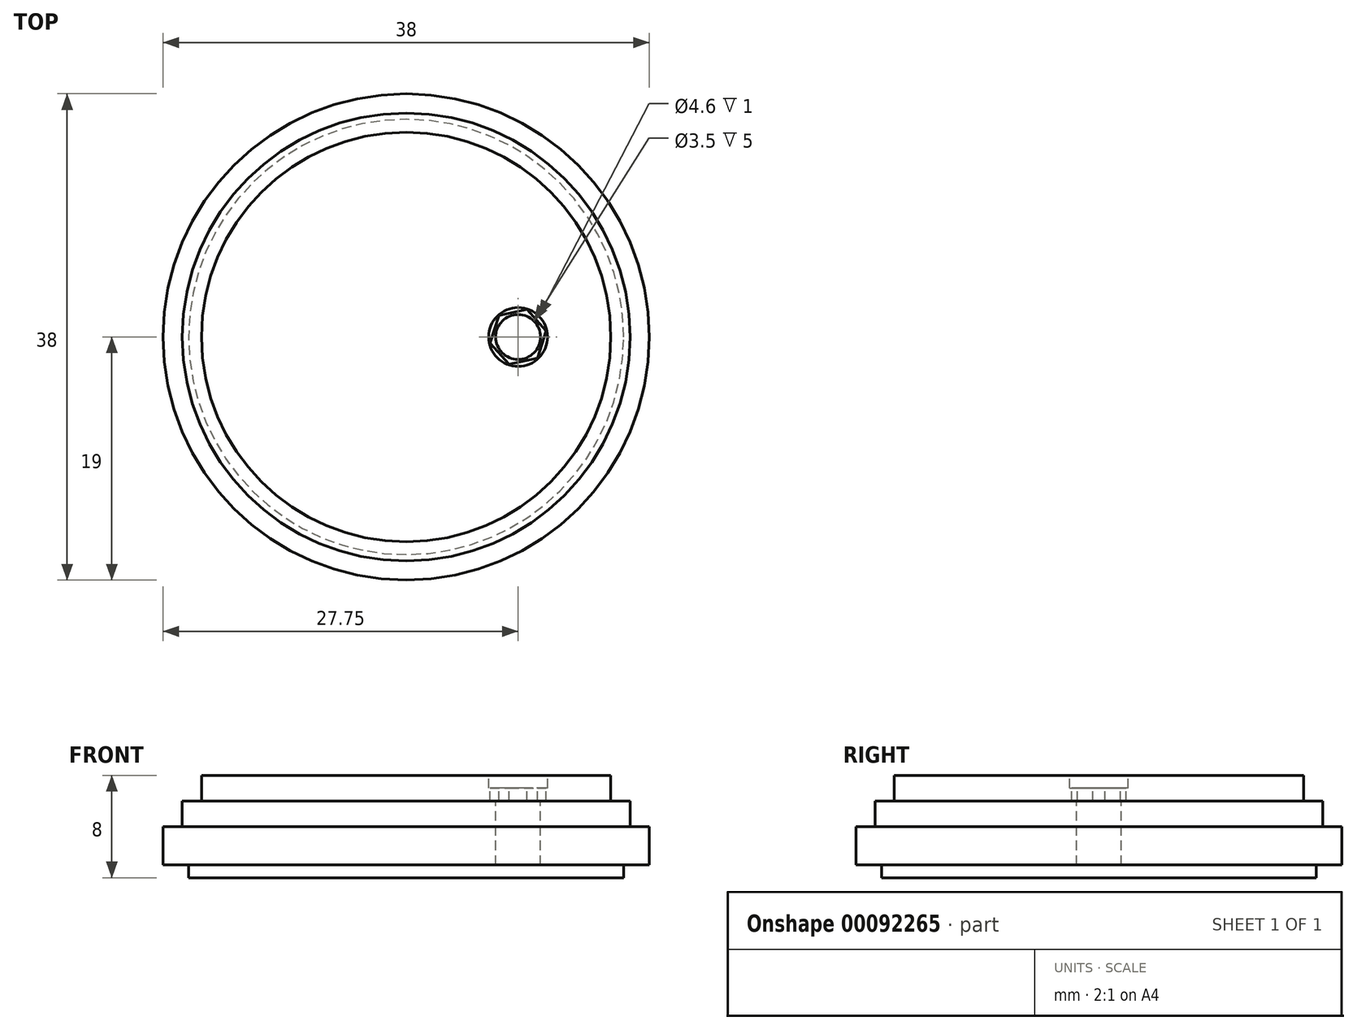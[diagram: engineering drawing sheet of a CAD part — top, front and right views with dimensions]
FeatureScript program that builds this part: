
annotation { "Feature Type Name" : "Feature", "Feature Type Description" : "" }
export const myFeature = defineFeature(function(context is Context, id is Id, definition is map)
    precondition{}
    {
        {
            var Q0;
            Q0=qCreatedBy(makeId("Front.planeOp"),FACE);
            var sketch = newSketch(context, id + "F0", { "sketchPlane" : qUnion([Q0])});
            skLineSegment(sketch, "E0", {"start": v(0, 0) * mm, "end": v(0, 8) * mm});
            skLineSegment(sketch, "E1", {"start": v(0, 8) * mm, "end": v(16, 8) * mm});
            skLineSegment(sketch, "E2", {"start": v(16, 8) * mm, "end": v(16, 6) * mm});
            skLineSegment(sketch, "E3", {"start": v(16, 6) * mm, "end": v(17.5, 6) * mm});
            skLineSegment(sketch, "E4", {"start": v(17.5, 6) * mm, "end": v(17.5, 4) * mm});
            skLineSegment(sketch, "E5", {"start": v(17.5, 4) * mm, "end": v(19, 4) * mm});
            skLineSegment(sketch, "E6", {"start": v(19, 4) * mm, "end": v(19, 1) * mm});
            skLineSegment(sketch, "E7", {"start": v(19, 1) * mm, "end": v(17, 1) * mm});
            skLineSegment(sketch, "E8", {"start": v(17, 1) * mm, "end": v(17, 0) * mm});
            skLineSegment(sketch, "E9", {"start": v(17, 0) * mm, "end": v(0, 0) * mm});
            skSolve(sketch);
        }
        {
            var Q0;
            Q0 = qSketchRegion(id + "F0", true);
            var Q1;
            Q1 = qConstructionFilter(qBodyType(qCreatedBy(id + "F0" ,EDGE), BodyType.WIRE), ConstructionObject.NO);
            var Q2;
            Q2=sQuery(id+"F0.wireOp",EDGE,"E0");
            revolve(context, id + "F1", {"entities" : qUnion([Q0]), "surfaceEntities" : qUnion([Q1]), "axis" : qUnion([Q2]), "revolveType" : RevolveType.FULL});
        }
        {
            var Q0;
            Q0=makeQuery(id+"F1.opRevolve","SWEPT_FACE",FACE,{"disambiguationData":[OSD([sQuery(id+"F0.wireOp",EDGE,"E1")])]});
            var sketch = newSketch(context, id + "F2", { "sketchPlane" : qUnion([Q0])});
            skCircle(sketch, "E10", {"center": v(8.75, 0) * mm, "radius": 1.75 * mm});
            skSolve(sketch);
        }
        {
            var Q0;
            Q0 = qSketchRegion(id + "F2", true);
            extrude(context, id + "F3", {"entities" : qUnion([Q0]), "operationType" : NewBodyOperationType.REMOVE, "oppositeDirection" : true, "depth" : 7 * mm});
        }
        {
            var Q0;
            Q0=makeQuery(id+"F1.opRevolve","SWEPT_FACE",FACE,{"disambiguationData":[OSD([sQuery(id+"F0.wireOp",EDGE,"E1")])]});
            var sketch = newSketch(context, id + "F4", { "sketchPlane" : qUnion([Q0])});
            skCircle(sketch, "E11.cCircle", {"center": v(8.75, 0) * mm, "radius": 2.25 * mm, "construction": true});
            skLineSegment(sketch, "E11.0", {"start": v(10.95, 0.47) * mm, "end": v(10.26, -1.67) * mm});
            skLineSegment(sketch, "E11.1", {"start": v(10.26, -1.67) * mm, "end": v(8.06, -2.14) * mm});
            skLineSegment(sketch, "E11.2", {"start": v(8.06, -2.14) * mm, "end": v(6.55, -0.47) * mm});
            skLineSegment(sketch, "E11.3", {"start": v(6.55, -0.47) * mm, "end": v(7.24, 1.67) * mm});
            skLineSegment(sketch, "E11.4", {"start": v(7.24, 1.67) * mm, "end": v(9.44, 2.14) * mm});
            skLineSegment(sketch, "E11.5", {"start": v(9.44, 2.14) * mm, "end": v(10.95, 0.47) * mm});
            skSolve(sketch);
        }
        {
            var Q0;
            Q0=makeQuery(id+"F4.imprint","IMPRINT",FACE,{"disambiguationData":[TD([[makeQuery(id+"F4.imprint","IMPRINT",EDGE,{"derivedFrom":makeQuery(id+"F3.boolean.opBoolean","COPY",EDGE,{"derivedFrom":makeQuery(id+"F3.opExtrude","CAP_EDGE",EDGE,{"disambiguationData":[OSD([sQuery(id+"F2.wireOp",EDGE,"E10")])],"isStart":true})})}),1.0]])]});
            var Q1;
            Q1 = qSketchRegion(id + "F4", true);
            extrude(context, id + "F5", {"entities" : qUnion([Q0, Q1]), "operationType" : NewBodyOperationType.REMOVE, "oppositeDirection" : true, "depth" : 2 * mm});
        }
        {
            var Q0;
            Q0=makeQuery(id+"F1.opRevolve","SWEPT_FACE",FACE,{"disambiguationData":[OSD([sQuery(id+"F0.wireOp",EDGE,"E1")])]});
            var sketch = newSketch(context, id + "F6", { "sketchPlane" : qUnion([Q0])});
            skCircle(sketch, "E12", {"center": v(8.75, 0) * mm, "radius": 2.3 * mm});
            skSolve(sketch);
        }
        {
            var Q0;
            Q0 = qSketchRegion(id + "F6", true);
            extrude(context, id + "F7", {"entities" : qUnion([Q0]), "operationType" : NewBodyOperationType.REMOVE, "oppositeDirection" : true, "depth" : 1 * mm});
        }
    });
